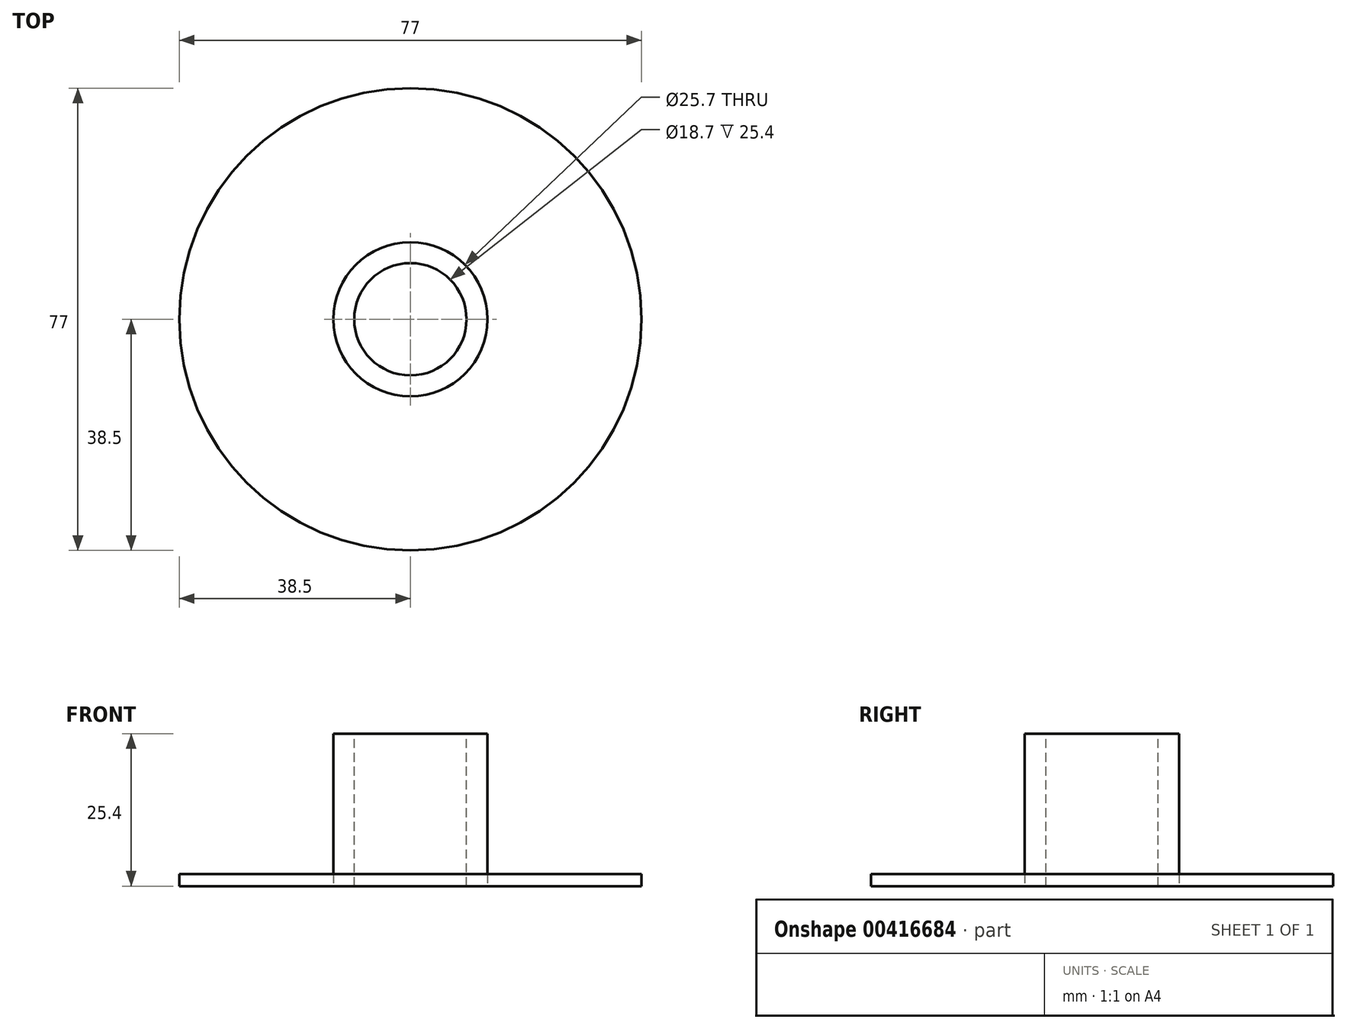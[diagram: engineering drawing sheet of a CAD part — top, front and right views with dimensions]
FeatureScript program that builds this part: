
annotation { "Feature Type Name" : "Feature", "Feature Type Description" : "" }
export const myFeature = defineFeature(function(context is Context, id is Id, definition is map)
    precondition{}
    {
        {
            var Q0;
            Q0=qCreatedBy(makeId("Top.planeOp"),FACE);
            var sketch = newSketch(context, id + "F0", { "sketchPlane" : qUnion([Q0])});
            skCircle(sketch, "E0", {"center": v(0, 0) * mm, "radius": 12.85 * mm});
            skSolve(sketch);
        }
        {
            var Q0;
            Q0=makeQuery(id+"F0.imprint","IMPRINT",FACE,{"disambiguationData":[TD([[makeQuery(id+"F0.imprint","IMPRINT",EDGE,{"derivedFrom":sQuery(id+"F0.wireOp",EDGE,"E0")}),1.0]])]});
            extrude(context, id + "F1", {"entities" : qUnion([Q0]), "depth" : 25.4 * mm, "offsetDistance" : 25 * mm});
        }
        {
            var Q0;
            Q0=makeQuery(id+"F1.opExtrude","CAP_FACE",FACE,{"disambiguationData":[OSD([sQuery(id+"F0.wireOp",EDGE,"E0")])],"isStart":true});
            var sketch = newSketch(context, id + "F2", { "sketchPlane" : qUnion([Q0])});
            skCircle(sketch, "E1", {"center": v(0, 0) * mm, "radius": 38.5 * mm});
            skSolve(sketch);
        }
        {
            var Q0;
            Q0=makeQuery(id+"F2.imprint","IMPRINT",FACE,{"disambiguationData":[TD([[makeQuery(id+"F2.imprint","IMPRINT",EDGE,{"derivedFrom":sQuery(id+"F2.wireOp",EDGE,"E1")}),1.0]])]});
            extrude(context, id + "F3", {"entities" : qUnion([Q0]), "oppositeDirection" : true, "depth" : 2 * mm, "offsetDistance" : 25 * mm});
        }
        {
            var Q0;
            Q0=makeQuery(id+"F1.opExtrude","CAP_FACE",FACE,{"disambiguationData":[OSD([sQuery(id+"F0.wireOp",EDGE,"E0")])],"isStart":false});
            var sketch = newSketch(context, id + "F4", { "sketchPlane" : qUnion([Q0])});
            skCircle(sketch, "E2", {"center": v(0, 0) * mm, "radius": 9.35 * mm});
            skSolve(sketch);
        }
        {
            var Q0;
            Q0=makeQuery(id+"F4.imprint","IMPRINT",FACE,{"disambiguationData":[TD([[makeQuery(id+"F4.imprint","IMPRINT",EDGE,{"derivedFrom":sQuery(id+"F4.wireOp",EDGE,"E2")}),1.0]])]});
            extrude(context, id + "F5", {"entities" : qUnion([Q0]), "operationType" : NewBodyOperationType.REMOVE, "oppositeDirection" : true, "depth" : 60 * mm, "offsetDistance" : 25 * mm});
        }
    });
